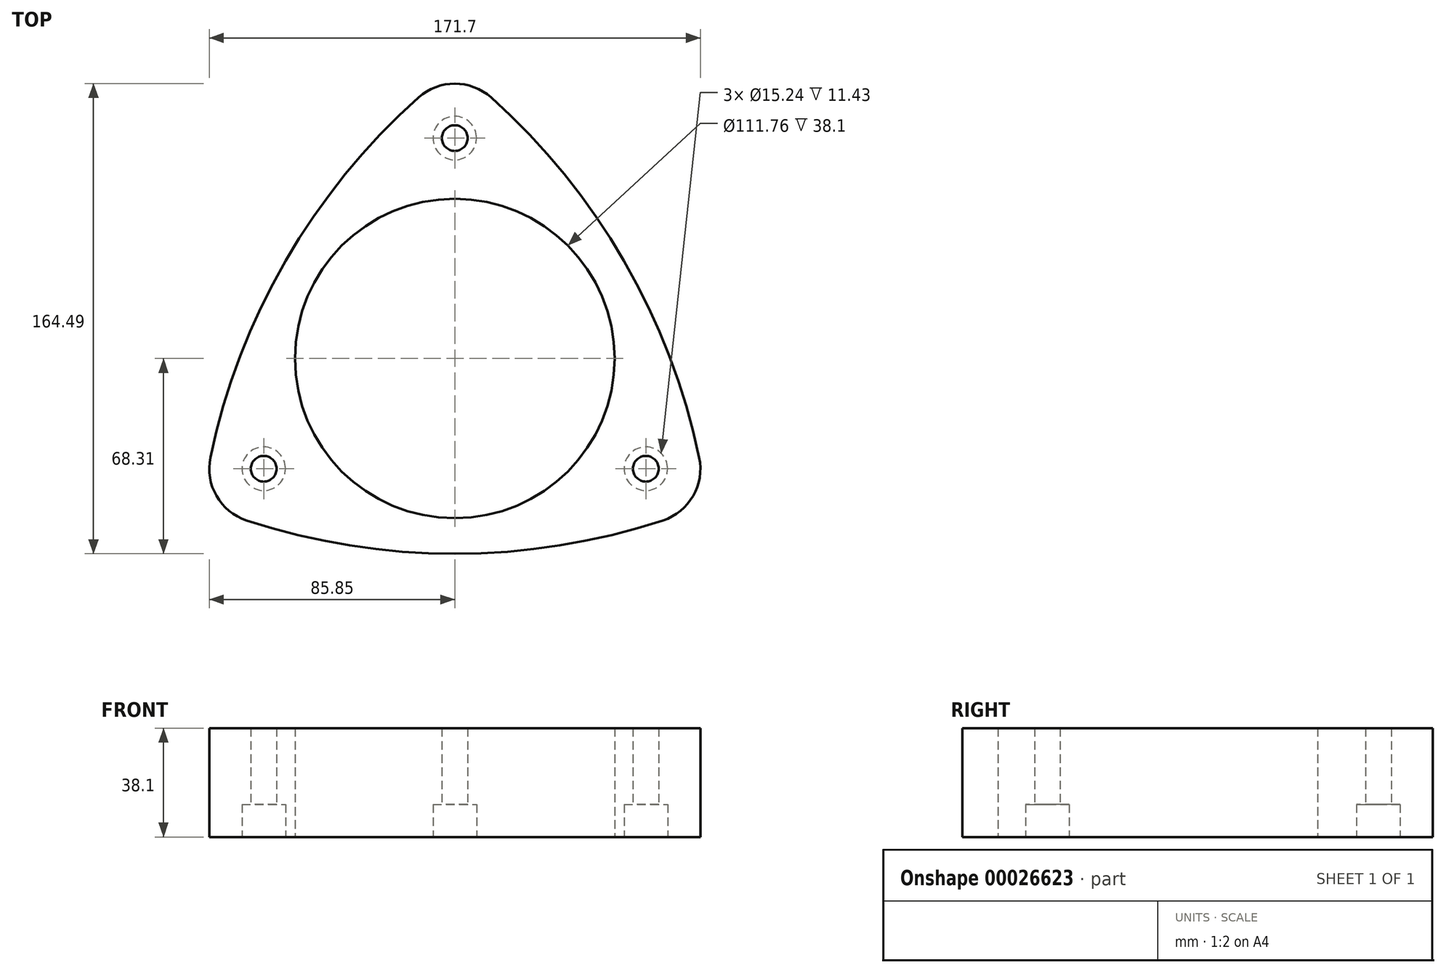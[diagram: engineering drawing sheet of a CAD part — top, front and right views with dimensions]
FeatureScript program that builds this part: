
annotation { "Feature Type Name" : "Feature", "Feature Type Description" : "" }
export const myFeature = defineFeature(function(context is Context, id is Id, definition is map)
    precondition{}
    {
        {
            var Q0;
            Q0=qCreatedBy(makeId("Top.planeOp"),FACE);
            var sketch = newSketch(context, id + "F0", { "sketchPlane" : qUnion([Q0])});
            skLineSegment(sketch, "E0", {"start": v(0, 77.13) * mm, "end": v(-66.8, -38.57) * mm, "construction": true});
            skLineSegment(sketch, "E1", {"start": v(-66.8, -38.57) * mm, "end": v(66.8, -38.57) * mm, "construction": true});
            skLineSegment(sketch, "E2", {"start": v(66.8, -38.57) * mm, "end": v(0, 77.13) * mm, "construction": true});
            skCircle(sketch, "E3", {"center": v(0, 77.13) * mm, "radius": 4.5 * mm});
            skCircle(sketch, "E4", {"center": v(-66.8, -38.57) * mm, "radius": 4.5 * mm});
            skCircle(sketch, "E5", {"center": v(66.8, -38.57) * mm, "radius": 4.5 * mm});
            skArc(sketch, "E6", {"start": v(-85.45, -34.67) * mm, "mid": v(-83.3, -48.1) * mm, "end": v(-72.75, -56.67) * mm});
            skArc(sketch, "E7", {"start": v(72.75, -56.67) * mm, "mid": v(83.3, -48.1) * mm, "end": v(85.45, -34.67) * mm});
            skArc(sketch, "E8", {"start": v(-12.7, 91.33) * mm, "mid": v(-59.16, 34.16) * mm, "end": v(-85.45, -34.67) * mm});
            skArc(sketch, "E9", {"start": v(85.45, -34.67) * mm, "mid": v(59.16, 34.16) * mm, "end": v(12.7, 91.33) * mm});
            skArc(sketch, "E10", {"start": v(-72.75, -56.67) * mm, "mid": v(0, -68.31) * mm, "end": v(72.75, -56.67) * mm});
            skArc(sketch, "E11", {"start": v(12.7, 91.33) * mm, "mid": v(0, 96.18) * mm, "end": v(-12.7, 91.33) * mm});
            skLineSegment(sketch, "E12", {"start": v(0, 77.13) * mm, "end": v(0, 0) * mm, "construction": true});
            skLineSegment(sketch, "E13", {"start": v(66.8, -38.57) * mm, "end": v(-33.4, 19.28) * mm, "construction": true});
            skLineSegment(sketch, "E14", {"start": v(-66.8, -38.57) * mm, "end": v(33.4, 19.28) * mm, "construction": true});
            skCircle(sketch, "E15", {"center": v(0, 0) * mm, "radius": 55.88 * mm});
            skSolve(sketch);
        }
        {
            var Q0;
            Q0 = qSketchRegion(id + "F0", true);
            extrude(context, id + "F1", {"entities" : qUnion([Q0]), "depth" : 38.1 * mm});
        }
        {
            var Q0;
            Q0=makeQuery(id+"F1.opExtrude","CAP_FACE",FACE,{"disambiguationData":[OSD([sQuery(id+"F0.wireOp",EDGE,"E3"),sQuery(id+"F0.wireOp",EDGE,"E4"),sQuery(id+"F0.wireOp",EDGE,"E5"),sQuery(id+"F0.wireOp",EDGE,"E6"),sQuery(id+"F0.wireOp",EDGE,"E7"),sQuery(id+"F0.wireOp",EDGE,"E8"),sQuery(id+"F0.wireOp",EDGE,"E9"),sQuery(id+"F0.wireOp",EDGE,"E10"),sQuery(id+"F0.wireOp",EDGE,"E11"),sQuery(id+"F0.wireOp",EDGE,"E15")])],"isStart":true});
            var sketch = newSketch(context, id + "F2", { "sketchPlane" : qUnion([Q0])});
            skCircle(sketch, "E16", {"center": v(-66.8, 38.57) * mm, "radius": 7.62 * mm});
            skCircle(sketch, "E17", {"center": v(66.8, 38.57) * mm, "radius": 7.62 * mm});
            skCircle(sketch, "E18", {"center": v(0, -77.13) * mm, "radius": 7.62 * mm});
            skSolve(sketch);
        }
        {
            var Q0;
            Q0=makeQuery(id+"F2.imprint","IMPRINT",FACE,{"disambiguationData":[TD([[makeQuery(id+"F2.imprint","IMPRINT",EDGE,{"derivedFrom":sQuery(id+"F2.wireOp",EDGE,"E16")}),1.0]])]});
            var Q1;
            Q1=makeQuery(id+"F2.imprint","IMPRINT",FACE,{"disambiguationData":[TD([[makeQuery(id+"F2.imprint","IMPRINT",EDGE,{"derivedFrom":sQuery(id+"F2.wireOp",EDGE,"E17")}),1.0]])]});
            var Q2;
            Q2=makeQuery(id+"F2.imprint","IMPRINT",FACE,{"disambiguationData":[TD([[makeQuery(id+"F2.imprint","IMPRINT",EDGE,{"derivedFrom":sQuery(id+"F2.wireOp",EDGE,"E18")}),1.0]])]});
            extrude(context, id + "F3", {"entities" : qUnion([Q0, Q1, Q2]), "operationType" : NewBodyOperationType.REMOVE, "oppositeDirection" : true, "depth" : 11.43 * mm});
        }
    });
